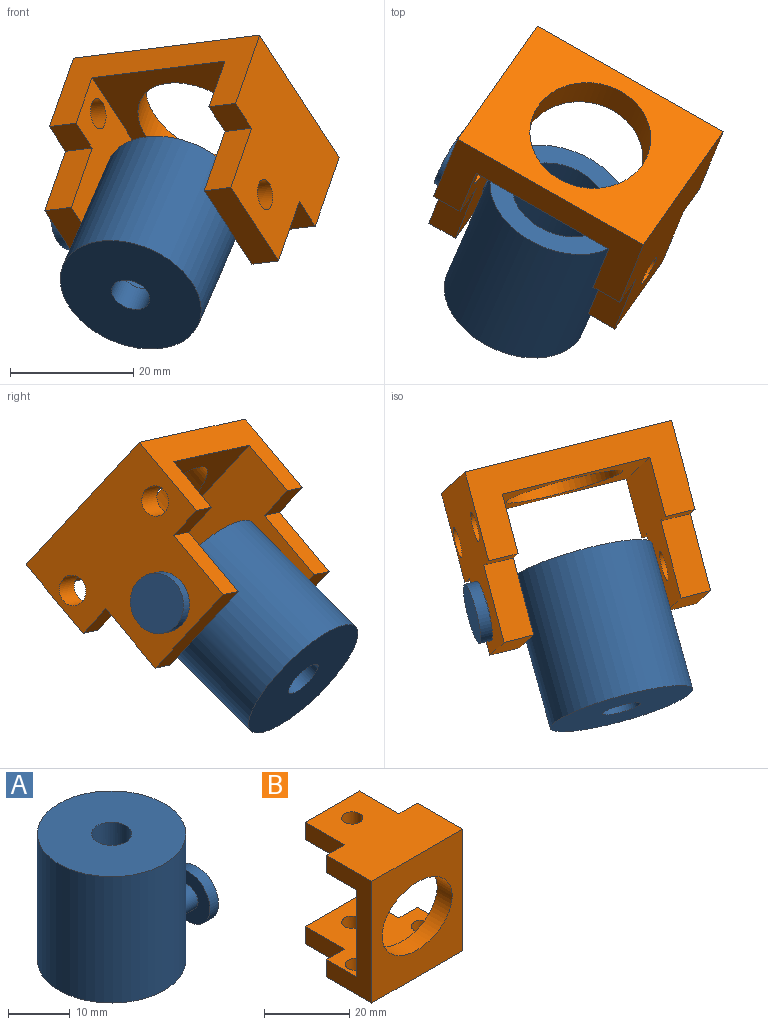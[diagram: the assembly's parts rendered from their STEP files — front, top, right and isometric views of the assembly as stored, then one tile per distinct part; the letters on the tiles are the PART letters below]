
ASSEMBLY  parts=2 mates=1
PART A: 10 faces, bbox 31.5x24x26.1 mm
  f0: cylinder r=12mm len=25mm, axis (0,0,-1), area 1869mm2, adj f1,f2,f6
  f1: plane 24x24mm, normal (0,0,1), area 419.2mm2, adj f0,f5
  f2: plane 24x24mm, normal (0,0,-1), area 245mm2, adj f0,f3
  f3: cylinder r=8.12mm len=20mm, axis (0,0,-1), area 1021mm2, adj f2,f4
  f4: plane 16.25x16.25mm, normal (0,0,-1), area 174.2mm2, adj f3,f5
  f5: cylinder r=3.25mm len=6.5mm, axis (0,0,1), area 102.1mm2, adj f1,f4
  f6: cylinder r=2.25mm len=5.71mm, axis (-1,0,0), area 79.3mm2, adj f0,f9
  f7: cylinder r=4.95mm len=9.91mm, axis (-1,0,0), area 62.3mm2, adj f8,f9
  f8: plane 9.91x9.91mm, normal (1,0,0), area 77.1mm2, adj f7
  f9: plane 9.91x9.91mm, normal (-1,0,0), area 61.2mm2, adj f6,f7
PART B: 23 faces, bbox 30.1x28x35 mm
  f0: plane 6.07x5mm, normal (0,1,0), area 30.3mm2, adj f9,f12,f13,f15
  f1: plane 18x5mm, normal (0,1,0), area 90mm2, adj f2,f3,f4,f5
  f2: plane 13x5mm, normal (-1,0,0), area 65mm2, adj f1,f4,f5,f6
  f3: plane 13x5mm, normal (1,0,0), area 65mm2, adj f1,f4,f5,f7
  f4: plane 30.07x28mm, normal (0,0,1), area 665.4mm2, adj f1,f2,f3,f6,f7,f8,f9,f11
  f5: plane 30.07x23mm, normal (0,0,-1), area 515mm2, adj f1,f2,f3,f6,f7,f8,f9,f10
  f6: plane 6x5mm, normal (0,1,0), area 30mm2, adj f2,f4,f5,f8
  f7: plane 6.07x5mm, normal (0,1,0), area 30.3mm2, adj f3,f4,f5,f9
  f8: plane 35x15mm, normal (-1,0,0), area 275mm2, adj f4,f5,f6,f10,f11,f12,f13,f14
  f9: plane 35x15mm, normal (1,0,0), area 275mm2, adj f0,f4,f5,f7,f10,f11,f12,f13
  f10: plane 30.07x25mm, normal (0,1,0), area 394.1mm2, adj f5,f8,f9,f13,f22
  f11: plane 35x30.07mm, normal (0,-1,0), area 694.8mm2, adj f4,f8,f9,f12,f22
  f12: plane 30.07x28mm, normal (0,0,-1), area 626.2mm2, adj f0,f8,f9,f11,f14,f15,f16,f17
  f13: plane 30.07x23mm, normal (0,0,1), area 475.9mm2, adj f0,f8,f9,f10,f14,f15,f16,f17
  f14: plane 5.99x5mm, normal (0,1,0), area 30mm2, adj f8,f12,f13,f16
  f15: plane 13x5mm, normal (1,0,0), area 65mm2, adj f0,f12,f13,f17
  f16: plane 13x5mm, normal (-1,0,0), area 65mm2, adj f12,f13,f14,f17
  f17: plane 18.01x5mm, normal (0,1,0), area 90mm2, adj f12,f13,f15,f16
  f18: cylinder r=2.5mm len=5mm, axis (0,0,-1), area 78.5mm2, adj f12,f13
  f19: cylinder r=2.5mm len=5mm, axis (0,0,-1), area 78.5mm2, adj f12,f13
  f20: cylinder r=2.5mm len=5mm, axis (0,0,-1), area 78.5mm2, adj f12,f13
  f21: cylinder r=2.5mm len=5mm, axis (0,0,1), area 78.5mm2, adj f4,f5
  f22: extruded ~23.29x19.55mm, area 337.1mm2, adj f10,f11
PLACE A rot(axis=(-0.26,-0.88,0.4),173.8deg) t=(-130.61,128.81,-8.52)mm
PLACE B rot(axis=(-0.52,0.42,-0.74),166.2deg) t=(-129.01,111.68,21.12)mm fixed
MATE revolute A.f6 <-> B.f20  axis (-0.86,0.49,-0.11) through (-148.61,135.81,-13.24)mm
